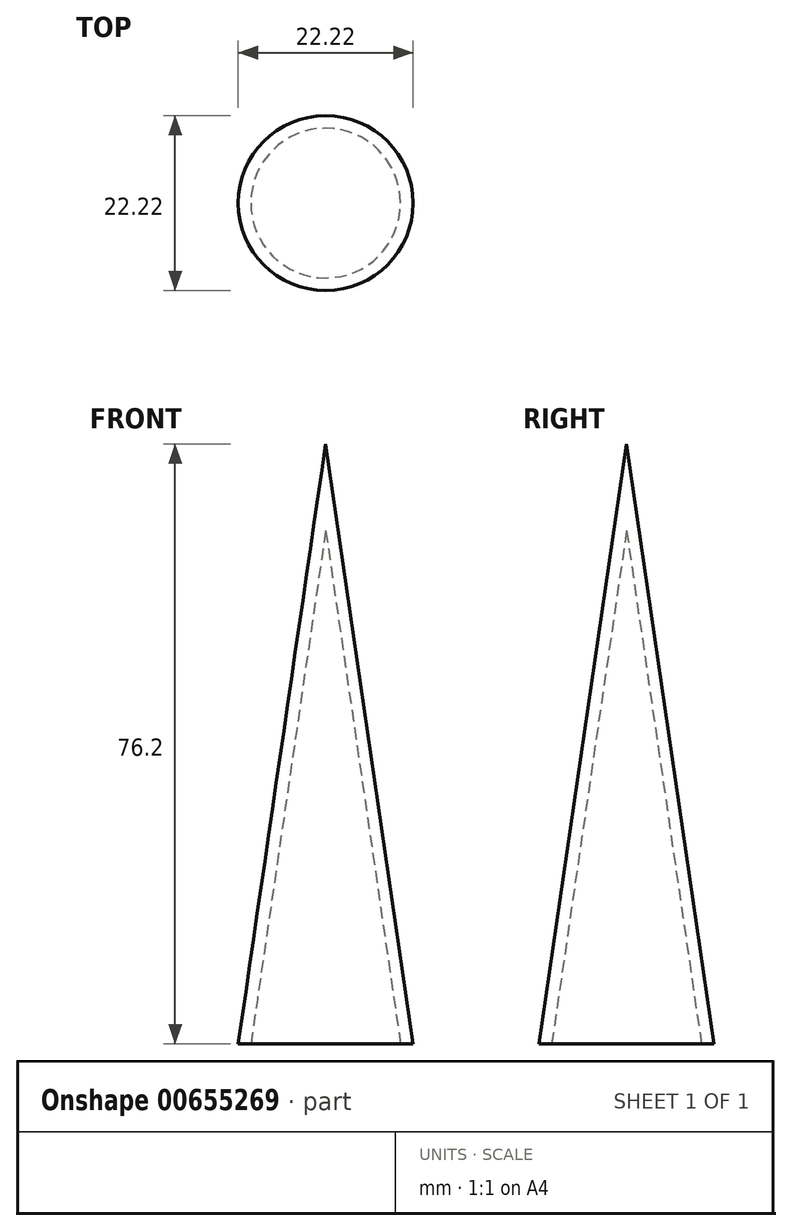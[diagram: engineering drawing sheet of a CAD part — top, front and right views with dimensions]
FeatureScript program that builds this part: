
annotation { "Feature Type Name" : "Feature", "Feature Type Description" : "" }
export const myFeature = defineFeature(function(context is Context, id is Id, definition is map)
    precondition{}
    {
        {
            var Q0;
            Q0=qCreatedBy(makeId("Front.planeOp"),FACE);
            var sketch = newSketch(context, id + "F0", { "sketchPlane" : qUnion([Q0])});
            skLineSegment(sketch, "E0", {"start": v(-40.96, 6.97) * mm, "end": v(-39.36, 6.97) * mm});
            skLineSegment(sketch, "E1", {"start": v(-29.85, 83.17) * mm, "end": v(-40.96, 6.97) * mm});
            skLineSegment(sketch, "E2.0", {"start": v(-29.85, 72.17) * mm, "end": v(-39.36, 6.97) * mm});
            skLineSegment(sketch, "E3", {"start": v(-29.85, 83.17) * mm, "end": v(-29.85, 72.17) * mm});
            skSolve(sketch);
        }
        {
            var Q0;
            Q0=makeQuery(id+"F0.imprint","IMPRINT",FACE,{"disambiguationData":[TD([[makeQuery(id+"F0.imprint","IMPRINT",EDGE,{"derivedFrom":sQuery(id+"F0.wireOp",EDGE,"E0")}),1.0]])]});
            var Q1;
            Q1=sQuery(id+"F0.wireOp",EDGE,"E3");
            revolve(context, id + "F1", {"entities" : qUnion([Q0]), "axis" : qUnion([Q1]), "revolveType" : RevolveType.FULL});
        }
    });
